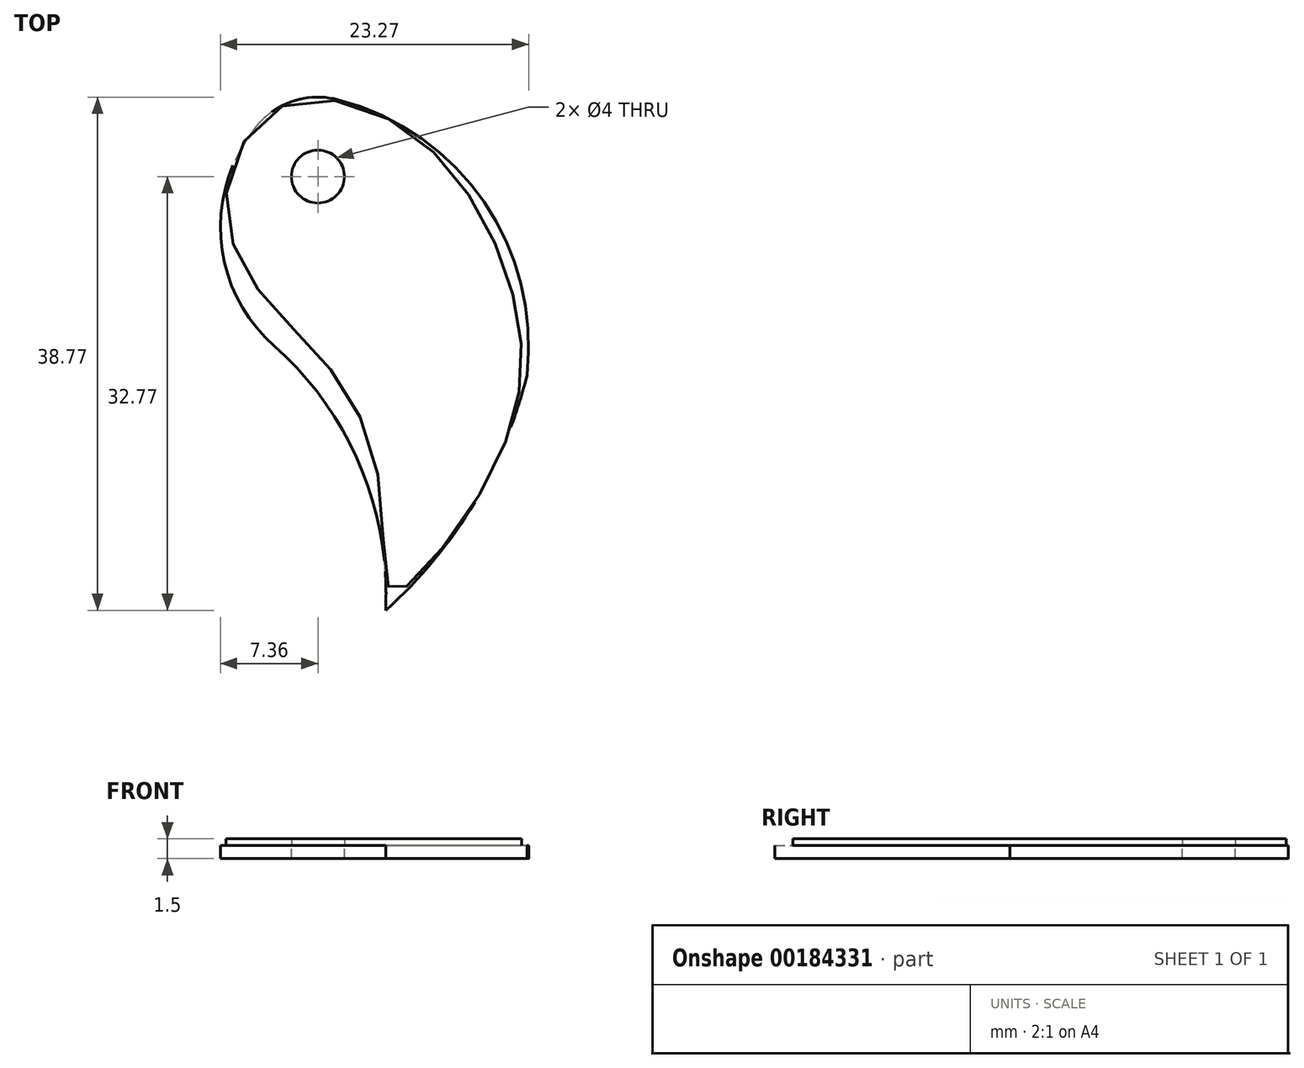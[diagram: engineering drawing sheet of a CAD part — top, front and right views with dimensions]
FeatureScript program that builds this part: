
annotation { "Feature Type Name" : "Feature", "Feature Type Description" : "" }
export const myFeature = defineFeature(function(context is Context, id is Id, definition is map)
    precondition{}
    {
        {
            var Q0;
            Q0=qCreatedBy(makeId("Top.planeOp"),FACE);
            var sketch = newSketch(context, id + "F0", { "sketchPlane" : qUnion([Q0])});
            skCircle(sketch, "E0", {"center": v(0, 0) * mm, "radius": 6 * mm});
            skCircle(sketch, "E1", {"center": v(4.64, -3.8) * mm, "radius": 12 * mm});
            skCircle(sketch, "E2", {"center": v(-19.86, -31.53) * mm, "radius": 25 * mm});
            skCircle(sketch, "E3", {"center": v(-18.38, -6.57) * mm, "radius": 35.19 * mm});
            skCircle(sketch, "E4", {"center": v(-3.3, -12.8) * mm, "radius": 19.21 * mm});
            skPoint(sketch, "E5", {"position": v(15.78, -15.02) * mm});
            skSolve(sketch);
        }
        {
            var Q0;
            {var subQ0=sQuery(id+"F0.wireOp",EDGE,"E0");var subQ1=makeQuery(id+"F0.imprint","INTERSECT",VERTEX,{"derivedFrom":[subQ0,sQuery(id+"F0.wireOp",EDGE,"fbEogU7R-LQS1-NTjB-gc15-IBQGo5zvZXqz")]});Q0=makeQuery(id+"F0.imprint","IMPRINT",FACE,{"disambiguationData":[TD([[makeQuery(id+"F0.imprint","IMPRINT",EDGE,{"disambiguationData":[TD([[subQ1,-1.0]])],"derivedFrom":subQ0}),1.0]])]});}
            var Q1;
            {var subQ1=sQuery(id+"F0.wireOp",EDGE,"4cnAOVYo-8zAc-2Clq-3g81-TC65WYo42Mdf");Q1=makeQuery(id+"F0.imprint","IMPRINT",FACE,{"disambiguationData":[TD([[makeQuery(id+"F0.imprint","IMPRINT",EDGE,{"derivedFrom":subQ1}),-1.0]])]});}
            var Q2;
            {var subQ6=sQuery(id+"F0.wireOp",EDGE,"4cnAOVYo-8zAc-2Clq-3g81-TC65WYo42Mdf");Q2=makeQuery(id+"F0.imprint","IMPRINT",FACE,{"disambiguationData":[TD([[makeQuery(id+"F0.imprint","IMPRINT",EDGE,{"derivedFrom":subQ6}),1.0]])]});}
            var Q3;
            {var subQ0=sQuery(id+"F0.wireOp",EDGE,"E1");var subQ1=sQuery(id+"F0.wireOp",EDGE,"E0");var subQ2=makeQuery(id+"F0.imprint","INTERSECT",VERTEX,{"derivedFrom":[subQ1,subQ0]});Q3=makeQuery(id+"F0.imprint","IMPRINT",FACE,{"disambiguationData":[TD([[makeQuery(id+"F0.imprint","IMPRINT",EDGE,{"disambiguationData":[TD([[subQ2,-1.0]])],"derivedFrom":subQ1}),-1.0]])]});}
            var Q4;
            {var subQ4=sQuery(id+"F0.wireOp",EDGE,"E2");var subQ5=sQuery(id+"F0.wireOp",EDGE,"E1");var subQ6=makeQuery(id+"F0.imprint","INTERSECT",VERTEX,{"derivedFrom":[subQ5,subQ4]});Q4=makeQuery(id+"F0.imprint","IMPRINT",FACE,{"disambiguationData":[TD([[makeQuery(id+"F0.imprint","IMPRINT",EDGE,{"disambiguationData":[TD([[subQ6,-1.0]])],"derivedFrom":subQ5}),-1.0]])]});}
            var Q5;
            {var subQ0=sQuery(id+"F0.wireOp",EDGE,"E3");var subQ1=sQuery(id+"F0.wireOp",EDGE,"E2");var subQ2=makeQuery(id+"F0.imprint","INTERSECT",VERTEX,{"disambiguationData":[OD(1.0)],"derivedFrom":[subQ1,subQ0]});Q5=makeQuery(id+"F0.imprint","IMPRINT",FACE,{"disambiguationData":[TD([[makeQuery(id+"F0.imprint","IMPRINT",EDGE,{"disambiguationData":[TD([[subQ2,-1.0]])],"derivedFrom":subQ1}),-1.0]])]});}
            extrude(context, id + "F1", {"entities" : qUnion([Q0, Q1, Q2, Q3, Q4, Q5]), "oppositeDirection" : true, "depth" : 1 * mm});
        }
        {
            var Q0;
            Q0=sQuery(id+"F0.wireOp",VERTEX,"E0.center");
            var Q1;
            Q1=makeQuery(id+"F1.opExtrude","SWEPT_BODY",BODY,{"disambiguationData":[OSD([sQuery(id+"F0.wireOp",EDGE,"E1"),sQuery(id+"F0.wireOp",EDGE,"E2"),sQuery(id+"F0.wireOp",EDGE,"E3")])]});
            hole(context, id + "F2", {"style" : HoleStyle.SIMPLE, "endStyle" : HoleEndStyle.THROUGH, "holeDiameter" : 4 * mm, "locations" : qUnion([Q0]), "scope" : qUnion([Q1]), "isTappedThrough" : true});
        }
        {
            var Q0;
            Q0=qCreatedBy(makeId("Top.planeOp"),FACE);
            var sketch = newSketch(context, id + "F3", { "sketchPlane" : qUnion([Q0])});
            skFitSpline(sketch, "E6", {"points": [v(-6.9, -1.25) * mm, v(-2.8, 5.28) * mm, v(5.24, 4.39) * mm, v(11.5, -1.58) * mm, v(14.8, -9.29) * mm, v(15.23, -16.05) * mm, v(12.15, -24.1) * mm, v(6.4, -31.17) * mm, v(5.42, -31.2) * mm, v(4.62, -23.11) * mm, v(0.85, -14.44) * mm, v(-4.72, -8.25) * mm, v(-6.9, -1.25) * mm]});
            skSolve(sketch);
        }
        {
            var Q0;
            Q0=makeQuery(id+"F3.imprint","IMPRINT",FACE,{"disambiguationData":[TD([[makeQuery(id+"F3.imprint","IMPRINT",EDGE,{"derivedFrom":sQuery(id+"F3.wireOp",EDGE,"E6")}),-1.0]])]});
            extrude(context, id + "F4", {"entities" : qUnion([Q0]), "depth" : .5 * mm});
        }
        {
            var Q0;
            Q0=sQuery(id+"F0.wireOp",VERTEX,"E0.center");
            var Q1;
            Q1=makeQuery(id+"F4.opExtrude","SWEPT_BODY",BODY,{"disambiguationData":[OSD([sQuery(id+"F3.wireOp",EDGE,"E6")])]});
            hole(context, id + "F5", {"style" : HoleStyle.SIMPLE, "endStyle" : HoleEndStyle.THROUGH, "oppositeDirection" : true, "holeDiameter" : 4 * mm, "locations" : qUnion([Q0]), "scope" : qUnion([Q1]), "isTappedThrough" : true});
        }
    });
